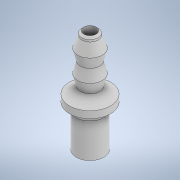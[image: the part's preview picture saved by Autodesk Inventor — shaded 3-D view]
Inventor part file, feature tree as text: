
AUTODESK INVENTOR PART (.ipt)
format: ipt  version: 2021 (Build 250183000, 183)  size: 142,336 bytes
history: native  units: in
note: dims shown in document units (in); Inventor stores cm internally (conversion verified against a paired STEP export)
features: revolve x1, sketch x1
ambient origin geometry x8: Origin, YZ Plane, XZ Plane, XY Plane, X Axis, Y Axis, Z Axis, Center Point
bodies: Solid1 (feature_tree)
feature tree (2):
  revolve  "Revolution1"  [1 undecoded]
  sketch  "Sketch1"  dims[d0=0.5906in d4=0.0394in d5=0.0354in d6=0.0709in d9=0.1969in d10=0.0394in d11=0.0394in d12=0.0984in d14=0.0787in d15=0.0472in d16=0.0709in d17=0.1181in d18=45.0deg d19=0.0118in d20=0.0551in d21=0.0551in d22=0.063in d23=0.063in d24=0.063in d26=90.0deg]
note: 1 required parameter value undecoded (feature->parameter linkage not recoverable at this tier; creation-order binding heuristic only, values carry confidence <= 0.55)
